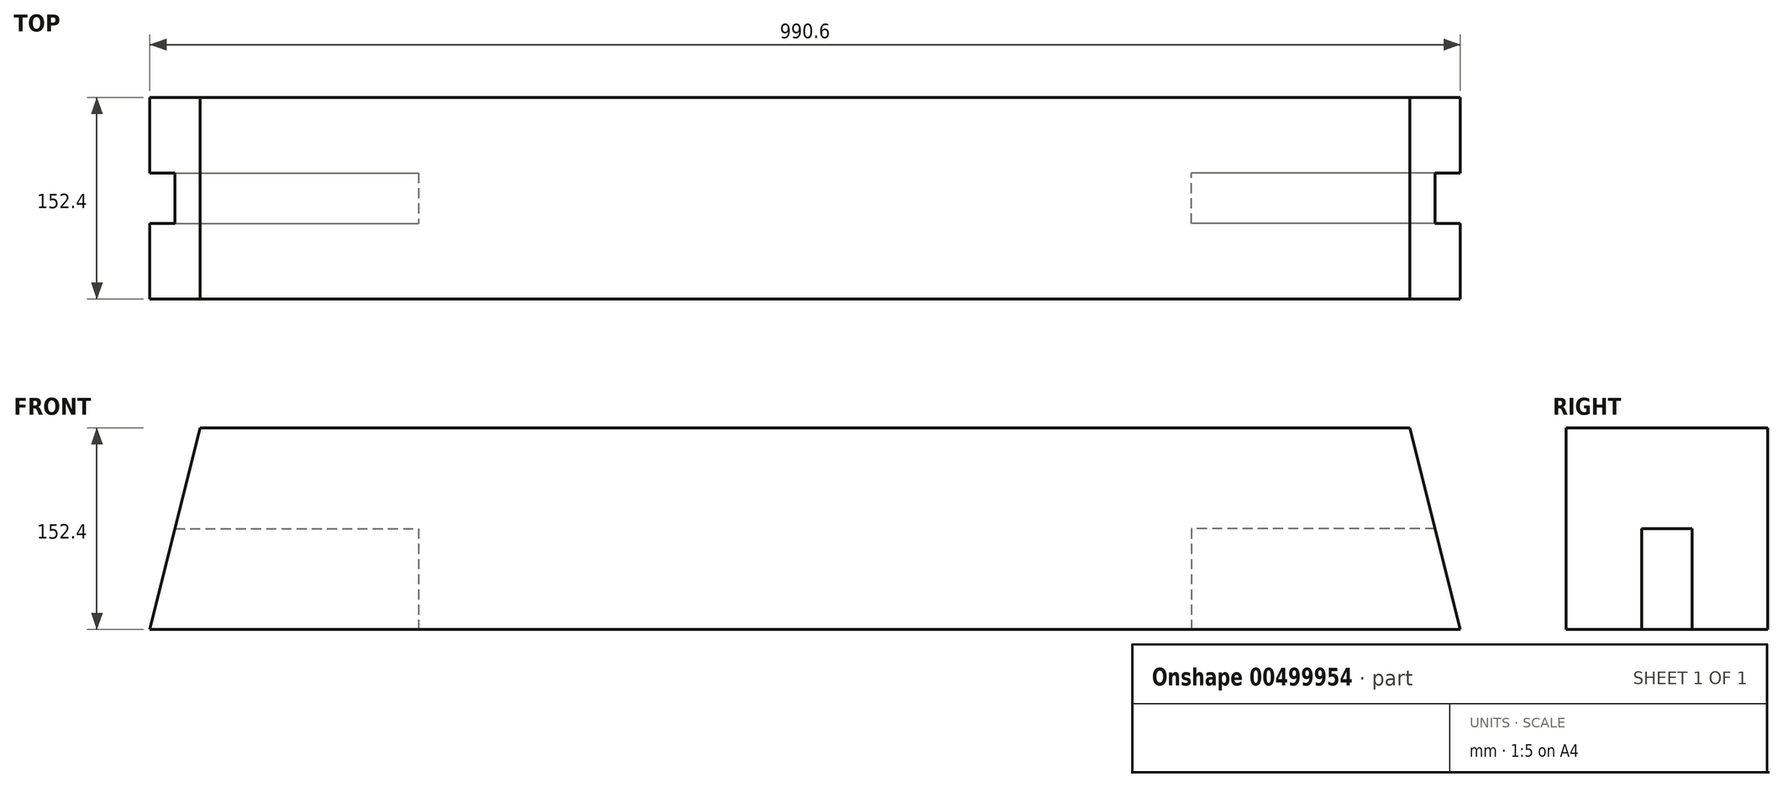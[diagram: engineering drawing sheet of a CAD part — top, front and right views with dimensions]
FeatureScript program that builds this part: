
annotation { "Feature Type Name" : "Feature", "Feature Type Description" : "" }
export const myFeature = defineFeature(function(context is Context, id is Id, definition is map)
    precondition{}
    {
        {
            var Q0;
            Q0=qCreatedBy(makeId("Front.planeOp"),FACE);
            var sketch = newSketch(context, id + "F0", { "sketchPlane" : qUnion([Q0])});
            skLineSegment(sketch, "E0.bottom", {"start": v(-495.3, 76.2) * mm, "end": v(495.3, 76.2) * mm});
            skLineSegment(sketch, "E0.top", {"start": v(-495.3, -76.2) * mm, "end": v(495.3, -76.2) * mm});
            skLineSegment(sketch, "E0.left", {"start": v(-495.3, 76.2) * mm, "end": v(-495.3, -76.2) * mm});
            skLineSegment(sketch, "E0.right", {"start": v(495.3, 76.2) * mm, "end": v(495.3, -76.2) * mm});
            skPoint(sketch, "E0.middle", {"position": v(0, 0) * mm});
            skLineSegment(sketch, "E1", {"start": v(-495.3, -76.2) * mm, "end": v(-457.2, 76.2) * mm});
            skLineSegment(sketch, "E2", {"start": v(495.3, -76.2) * mm, "end": v(457.2, 76.2) * mm});
            skSolve(sketch);
        }
        {
            var Q0;
            Q0=makeQuery(id+"F0.imprint","IMPRINT",FACE,{"disambiguationData":[TD([[makeQuery(id+"F0.imprint","IMPRINT",EDGE,{"derivedFrom":sQuery(id+"F0.wireOp",EDGE,"E0.top")}),1.0]])]});
            extrude(context, id + "F1", {"entities" : qUnion([Q0]), "depth" : 152.4 * mm, "offsetDistance" : 25.4 * mm});
        }
        {
            var Q0;
            Q0=makeQuery(id+"F1.opExtrude","SWEPT_FACE",FACE,{"disambiguationData":[OSD([sQuery(id+"F0.wireOp",EDGE,"E0.top")])]});
            var sketch = newSketch(context, id + "F2", { "sketchPlane" : qUnion([Q0])});
            skLineSegment(sketch, "E3.bottom", {"start": v(-495.3, 57.15) * mm, "end": v(-292.1, 57.15) * mm});
            skLineSegment(sketch, "E3.top", {"start": v(-495.3, 95.25) * mm, "end": v(-292.1, 95.25) * mm});
            skLineSegment(sketch, "E3.left", {"start": v(-495.3, 57.15) * mm, "end": v(-495.3, 95.25) * mm});
            skLineSegment(sketch, "E3.right", {"start": v(-292.1, 57.15) * mm, "end": v(-292.1, 95.25) * mm});
            skLineSegment(sketch, "E4.bottom", {"start": v(495.3, 95.25) * mm, "end": v(292.1, 95.25) * mm});
            skLineSegment(sketch, "E4.top", {"start": v(495.3, 57.15) * mm, "end": v(292.1, 57.15) * mm});
            skLineSegment(sketch, "E4.left", {"start": v(495.3, 95.25) * mm, "end": v(495.3, 57.15) * mm});
            skLineSegment(sketch, "E4.right", {"start": v(292.1, 95.25) * mm, "end": v(292.1, 57.15) * mm});
            skSolve(sketch);
        }
        {
            var Q0;
            Q0 = qSketchRegion(id + "F2", true);
            extrude(context, id + "F3", {"entities" : qUnion([Q0]), "operationType" : NewBodyOperationType.REMOVE, "oppositeDirection" : true, "depth" : 76.2 * mm, "offsetDistance" : 25.4 * mm});
        }
    });
